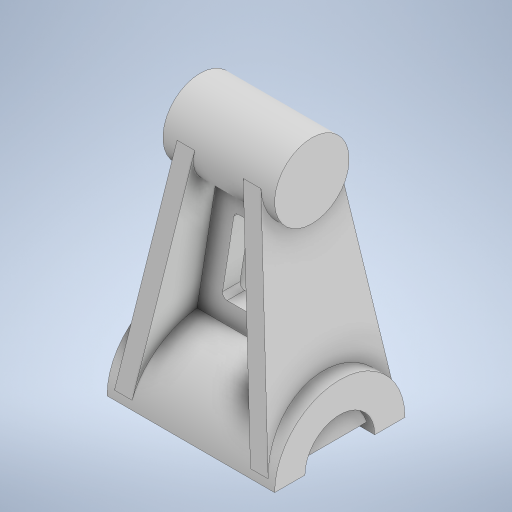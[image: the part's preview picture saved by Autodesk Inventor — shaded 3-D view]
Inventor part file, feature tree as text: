
AUTODESK INVENTOR PART (.ipt)
format: ipt  version: 2023 (Build 270158000, 158)  size: 357,376 bytes
history: native  units: mm
features: sketch x6, extrude x6, other x2, mirror x1
ambient origin geometry x8: Origin, YZ Plane, XZ Plane, XY Plane, X Axis, Y Axis, Z Axis, Center Point
bodies: Solido1 (feature_tree)
feature tree (15):
  sketch  "Schizzo1"
  extrude  "Estrusione1"  Depth=20.0mm
  extrude  "Estrusione2"  Depth=15.0mm
  sketch  "Schizzo3"
  other  "Piano di lavoro2"
  sketch  "Schizzo4"
  extrude  "Estrusione4"  Depth=96.0mm
  mirror  "Specchio1"
  sketch  "Schizzo8"
  extrude  "Estrusione5"  Depth=28.0mm
  extrude  "Estrusione6"  Depth=32.0mm
  extrude  "Estrusione7"  Depth=48.0mm TaperAngle=0.0deg
  sketch  "Schizzo6"
  other  "Linea chiusa proiettata1"
  sketch  "Schizzo9"
